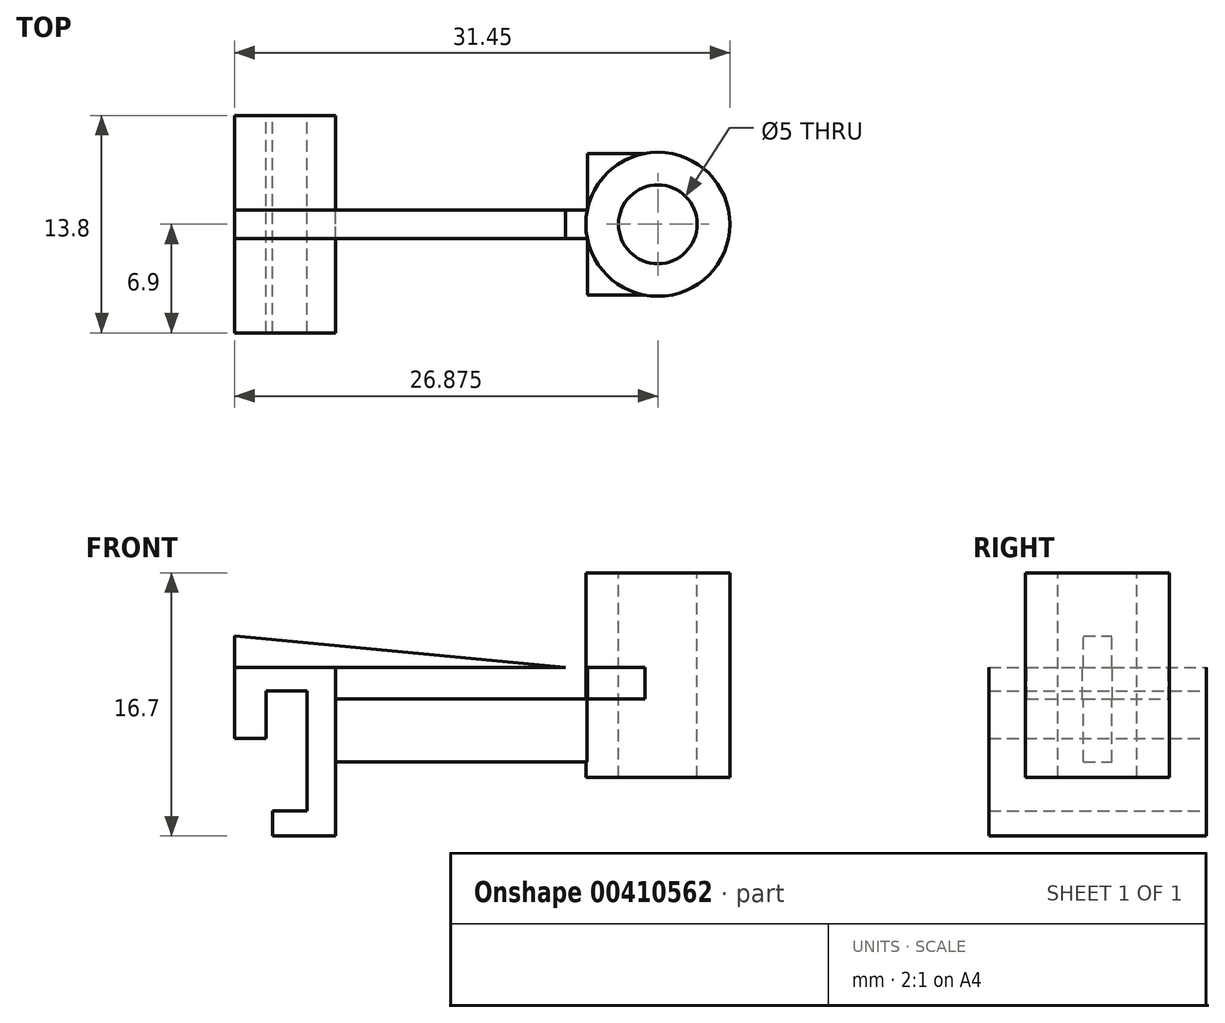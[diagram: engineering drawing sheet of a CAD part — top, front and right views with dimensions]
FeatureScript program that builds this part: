
annotation { "Feature Type Name" : "Feature", "Feature Type Description" : "" }
export const myFeature = defineFeature(function(context is Context, id is Id, definition is map)
    precondition{}
    {
        {
            var Q0;
            Q0=qCreatedBy(makeId("Front.planeOp"),FACE);
            var sketch = newSketch(context, id + "F0", { "sketchPlane" : qUnion([Q0])});
            skLineSegment(sketch, "E0.bottom", {"start": v(8, -2) * mm, "end": v(-8, -2) * mm});
            skLineSegment(sketch, "E0.top", {"start": v(8, 2) * mm, "end": v(-8, 2) * mm});
            skLineSegment(sketch, "E0.left", {"start": v(8, -2) * mm, "end": v(8, 2) * mm});
            skLineSegment(sketch, "E0.right", {"start": v(-8, -2) * mm, "end": v(-8, 2) * mm});
            skPoint(sketch, "E0.middle", {"position": v(0, 0) * mm});
            skLineSegment(sketch, "E1.bottom", {"start": v(8, -3) * mm, "end": v(15.6, -3) * mm});
            skLineSegment(sketch, "E1.top", {"start": v(8, 10) * mm, "end": v(15.6, 10) * mm});
            skLineSegment(sketch, "E1.left", {"start": v(8, -3) * mm, "end": v(8, 10) * mm});
            skLineSegment(sketch, "E2.bottom", {"start": v(12, 2) * mm, "end": v(-8, 2) * mm});
            skLineSegment(sketch, "E2.top", {"start": v(12, 4) * mm, "end": v(-8, 4) * mm});
            skLineSegment(sketch, "E2.left", {"start": v(12, 2) * mm, "end": v(12, 4) * mm});
            skLineSegment(sketch, "E2.right", {"start": v(-8, 2) * mm, "end": v(-8, 4) * mm});
            skLineSegment(sketch, "E3", {"start": v(-8, 4) * mm, "end": v(-8, -6.7) * mm});
            skLineSegment(sketch, "E4", {"start": v(-8, -6.7) * mm, "end": v(-12, -6.7) * mm});
            skLineSegment(sketch, "E5", {"start": v(-12, -6.7) * mm, "end": v(-12, -5.1) * mm});
            skLineSegment(sketch, "E6", {"start": v(-12, -5.1) * mm, "end": v(-9.8, -5.1) * mm});
            skLineSegment(sketch, "E7", {"start": v(-9.8, -5.1) * mm, "end": v(-9.8, 2.5) * mm});
            skLineSegment(sketch, "E8", {"start": v(-9.8, 2.5) * mm, "end": v(-12.4, 2.5) * mm});
            skLineSegment(sketch, "E9", {"start": v(-12.4, 2.5) * mm, "end": v(-12.4, -0.5) * mm});
            skLineSegment(sketch, "E10", {"start": v(-12.4, -0.5) * mm, "end": v(-14.4, -0.5) * mm});
            skLineSegment(sketch, "E11", {"start": v(-14.4, -0.5) * mm, "end": v(-14.4, 4) * mm});
            skLineSegment(sketch, "E12", {"start": v(-14.4, 4) * mm, "end": v(-8, 4) * mm});
            skLineSegment(sketch, "E13", {"start": v(-14.4, 4) * mm, "end": v(-14.4, 6) * mm});
            skLineSegment(sketch, "E14", {"start": v(-14.4, 6) * mm, "end": v(6.6, 4) * mm});
            skLineSegment(sketch, "E15", {"start": v(6.6, 4) * mm, "end": v(-14.4, 4) * mm});
            skLineSegment(sketch, "E16.bottom", {"start": v(8, 10) * mm, "end": v(12.5, 10) * mm});
            skLineSegment(sketch, "E16.top", {"start": v(8, -3) * mm, "end": v(12.5, -3) * mm});
            skLineSegment(sketch, "E16.left", {"start": v(8, 10) * mm, "end": v(8, -3) * mm});
            skLineSegment(sketch, "E16.right", {"start": v(12.5, 10) * mm, "end": v(12.5, -3) * mm});
            skLineSegment(sketch, "E17.bottom", {"start": v(8, 10) * mm, "end": v(17, 10) * mm});
            skLineSegment(sketch, "E17.top", {"start": v(8, -3) * mm, "end": v(17, -3) * mm});
            skLineSegment(sketch, "E17.right", {"start": v(17, 10) * mm, "end": v(17, -3) * mm});
            skSolve(sketch);
        }
        {
            var Q0;
            {var subQ5=sQuery(id+"F0.wireOp",EDGE,"E4");Q0=makeQuery(id+"F0.imprint","IMPRINT",FACE,{"disambiguationData":[TD([[makeQuery(id+"F0.imprint","IMPRINT",EDGE,{"derivedFrom":subQ5}),-1.0]])]});}
            extrude(context, id + "F1", {"entities" : qUnion([Q0]), "endBound" : BoundingType.SYMMETRIC, "depth" : 13.8 * mm});
        }
        {
            var Q0;
            {var subQ0=sQuery(id+"F0.wireOp",EDGE,"E0.bottom");Q0=makeQuery(id+"F0.imprint","IMPRINT",FACE,{"disambiguationData":[TD([[makeQuery(id+"F0.imprint","IMPRINT",EDGE,{"derivedFrom":subQ0}),-1.0]])]});}
            extrude(context, id + "F2", {"entities" : qUnion([Q0]), "operationType" : NewBodyOperationType.ADD, "endBound" : BoundingType.SYMMETRIC, "depth" : 1.8 * mm});
        }
        {
            var Q0;
            {var subQ0=sQuery(id+"F0.wireOp",EDGE,"E2.left");Q0=makeQuery(id+"F0.imprint","IMPRINT",FACE,{"disambiguationData":[TD([[makeQuery(id+"F0.imprint","IMPRINT",EDGE,{"derivedFrom":subQ0}),1.0]])]});}
            var Q1;
            {var subQ0=sQuery(id+"F0.wireOp",EDGE,"E3");var subQ1=sQuery(id+"F0.wireOp",EDGE,"E2.bottom");var subQ2=makeQuery(id+"F0.imprint","INTERSECT",VERTEX,{"derivedFrom":[subQ1,subQ0]});Q1=makeQuery(id+"F0.imprint","IMPRINT",FACE,{"disambiguationData":[TD([[makeQuery(id+"F0.imprint","IMPRINT",EDGE,{"disambiguationData":[TD([[subQ2,1.0]])],"derivedFrom":subQ1}),-1.0]])]});}
            extrude(context, id + "F3", {"entities" : qUnion([Q0, Q1]), "operationType" : NewBodyOperationType.ADD, "endBound" : BoundingType.SYMMETRIC, "depth" : 9 * mm});
        }
        {
            var Q0;
            {var subQ0=sQuery(id+"F0.wireOp",EDGE,"E13");Q0=makeQuery(id+"F0.imprint","IMPRINT",FACE,{"disambiguationData":[TD([[makeQuery(id+"F0.imprint","IMPRINT",EDGE,{"derivedFrom":subQ0}),-1.0]])]});}
            extrude(context, id + "F4", {"entities" : qUnion([Q0]), "operationType" : NewBodyOperationType.ADD, "endBound" : BoundingType.SYMMETRIC, "depth" : 1.8 * mm});
        }
        {
            var Q0;
            Q0=qCreatedBy(makeId("Top.planeOp"),FACE);
            var sketch = newSketch(context, id + "F5", { "sketchPlane" : qUnion([Q0])});
            skCircle(sketch, "E18", {"center": v(12.47, 0) * mm, "radius": 4.58 * mm});
            skSolve(sketch);
        }
        {
            var Q0;
            Q0=makeQuery(id+"F5.imprint","IMPRINT",FACE,{"disambiguationData":[TD([[makeQuery(id+"F5.imprint","IMPRINT",EDGE,{"derivedFrom":sQuery(id+"F5.wireOp",EDGE,"E18")}),1.0]])]});
            var Q1;
            Q1=sQuery(id+"F5.wireOp",EDGE,"E18");
            extrude(context, id + "F6", {"entities" : qUnion([Q0]), "operationType" : NewBodyOperationType.ADD, "surfaceEntities" : qUnion([Q1]), "oppositeDirection" : true, "depth" : 3 * mm, "hasSecondDirection" : true, "secondDirectionOppositeDirection" : false, "secondDirectionDepth" : 10 * mm});
        }
        {
            var Q0;
            Q0=sQuery(id+"F5.wireOp",VERTEX,"E18.center");
            var Q1;
            Q1=makeQuery(id+"F1.opExtrude","SWEPT_BODY",BODY,{"disambiguationData":[OSD([sQuery(id+"F0.wireOp",EDGE,"E3"),sQuery(id+"F0.wireOp",EDGE,"E4"),sQuery(id+"F0.wireOp",EDGE,"E5"),sQuery(id+"F0.wireOp",EDGE,"E6"),sQuery(id+"F0.wireOp",EDGE,"E7"),sQuery(id+"F0.wireOp",EDGE,"E8"),sQuery(id+"F0.wireOp",EDGE,"E9"),sQuery(id+"F0.wireOp",EDGE,"E10"),sQuery(id+"F0.wireOp",EDGE,"E11"),sQuery(id+"F0.wireOp",EDGE,"E15")])]});
            hole(context, id + "F7", {"style" : HoleStyle.SIMPLE, "endStyle" : HoleEndStyle.THROUGH, "holeDiameter" : 5 * mm, "isTappedThrough" : true, "tappedDepth" : 12 * mm, "tapClearance" : 3, "locations" : qUnion([Q0]), "scope" : qUnion([Q1])});
        }
        {
            var Q0;
            Q0=sQuery(id+"F5.wireOp",VERTEX,"E18.center");
            var Q1;
            Q1=makeQuery(id+"F1.opExtrude","SWEPT_BODY",BODY,{"disambiguationData":[OSD([sQuery(id+"F0.wireOp",EDGE,"E3"),sQuery(id+"F0.wireOp",EDGE,"E4"),sQuery(id+"F0.wireOp",EDGE,"E5"),sQuery(id+"F0.wireOp",EDGE,"E6"),sQuery(id+"F0.wireOp",EDGE,"E7"),sQuery(id+"F0.wireOp",EDGE,"E8"),sQuery(id+"F0.wireOp",EDGE,"E9"),sQuery(id+"F0.wireOp",EDGE,"E10"),sQuery(id+"F0.wireOp",EDGE,"E11"),sQuery(id+"F0.wireOp",EDGE,"E15")])]});
            hole(context, id + "F8", {"style" : HoleStyle.SIMPLE, "endStyle" : HoleEndStyle.THROUGH, "oppositeDirection" : true, "holeDiameter" : 5 * mm, "isTappedThrough" : true, "tappedDepth" : 12 * mm, "tapClearance" : 3, "locations" : qUnion([Q0]), "scope" : qUnion([Q1])});
        }
    });
